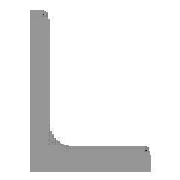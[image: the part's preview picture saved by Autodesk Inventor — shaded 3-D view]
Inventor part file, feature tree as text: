
AUTODESK INVENTOR PART (.ipt)
format: ipt  version: 2024.1 (Build 281209000, 209)  size: 133,120 bytes
history: native  units: mm (DEFAULTED — no unit token found)
features: other x4, plane x3, split x2, sketch x1
ambient origin geometry x8: Origin, YZ Plane, XZ Plane, XY Plane, X Axis, Y Axis, Z Axis, Center Point
bodies: Solid1 (feature_tree), Body (feature_tree)
feature tree (10):
  parser-record x1  (decoder bookkeeping rows leaked as tree rows — omitted from the tree; the rows remain in map.json)
  other  "Driven Length"
  other  "Start Plane"
  other  "End Plane"
  plane  "Work Plane4"
  split  "Split1"
  plane  "Work Plane5"
  split  "Split2"
  sketch  "Sketch3"  dims[d0=25.4mm d1=25.4mm d2=3.175mm d3=3.175mm d4=625.4mm d5=0.0mm d10=0.0mm d11=0.0mm d12=-12.7mm d13=612.7mm d14=3.302mm d15=1.524mm d16=90.0deg d17=625.4mm]
  plane  "Work Plane3"
